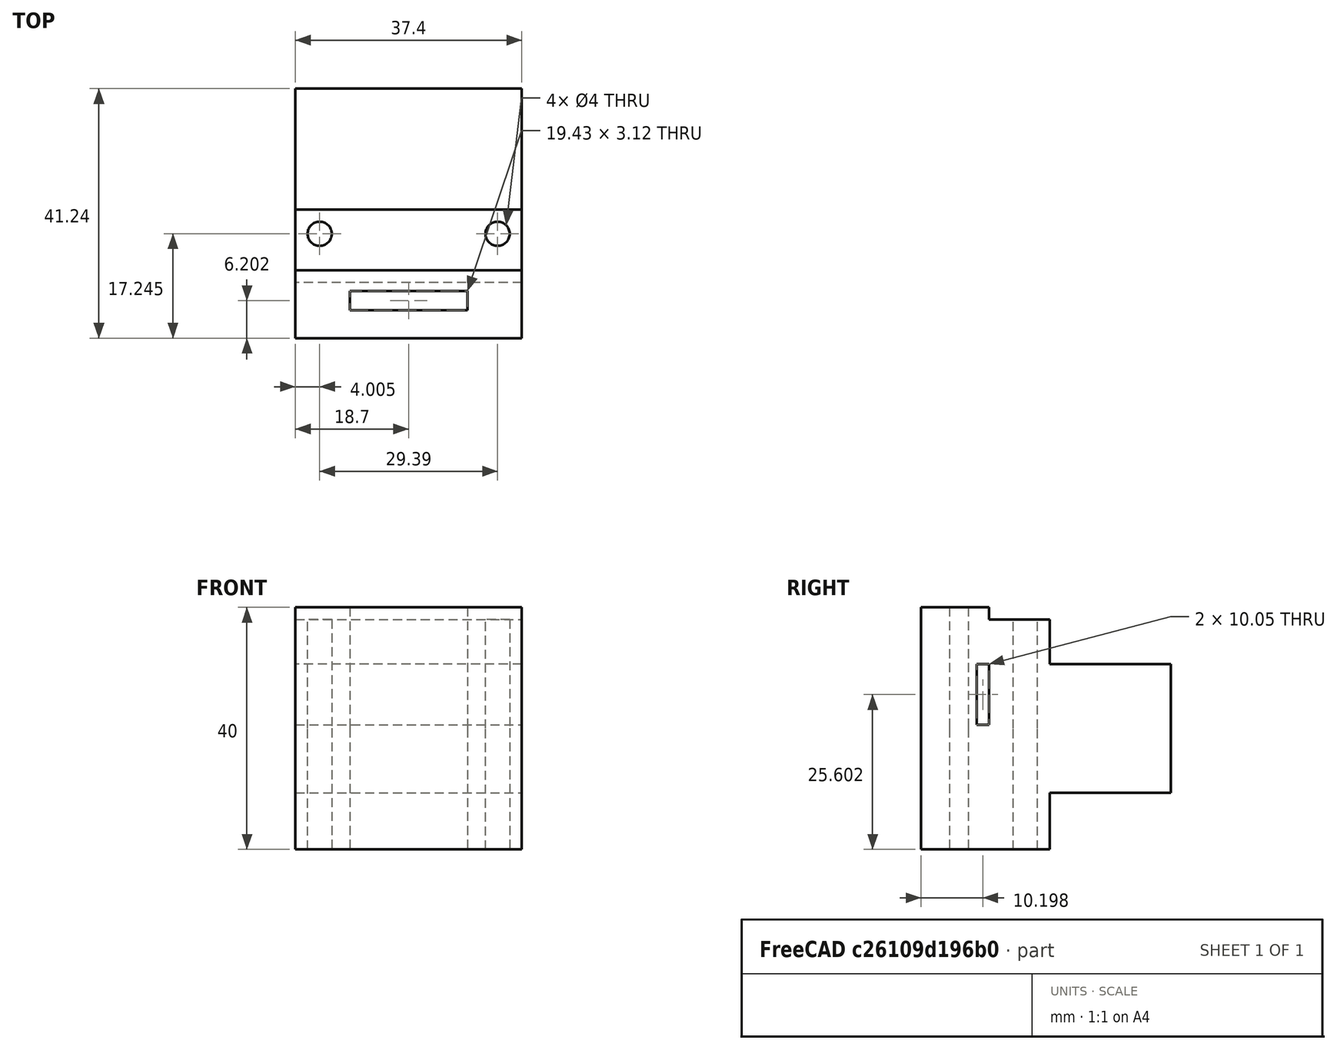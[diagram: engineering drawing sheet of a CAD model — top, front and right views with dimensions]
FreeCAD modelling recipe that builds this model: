
FCSTD DOCUMENT  (FreeCAD 0.17R13541 (Git))
Label: suporMicroSD
License: All rights reserved
LicenseURL: http://en.wikipedia.org/wiki/All_rights_reserved
objects: Sketcher::SketchObject×3, PartDesign::Body×1, PartDesign::Pad×1, PartDesign::Pocket×1
note: 8 computed .brp shape members not serialized (recipe doc carries the construction recipe); baked Part::Feature solids carry a one-line shape summary decoded from their .brp

FEATURE [PartDesign::Body] Body
  Group = -> [Sketch,Pad,Sketch001,Sketch003,Pocket001]
  Origin = -> Origin
  Tip = -> Pocket001
FEATURE [Sketcher::SketchObject] Sketch  label="base"
  MapMode = 5
  Placement = pos=(0,10.625,0) rot=(0,0.707107,0.707107;3.14159rad)
  Support = -> [Pocket001]
  sketch-geometry (4):
    g0: LineSegment StartX=-18.695 StartY=10.625 StartZ=0 EndX=18.695 EndY=10.625 EndZ=0
    g1: LineSegment StartX=18.695 StartY=10.625 StartZ=0 EndX=18.695 EndY=-10.625 EndZ=0
    g2: LineSegment StartX=18.695 StartY=-10.625 StartZ=0 EndX=-18.695 EndY=-10.625 EndZ=0
    g3: LineSegment StartX=-18.695 StartY=-10.625 StartZ=0 EndX=-18.695 EndY=10.625 EndZ=0
  constraints (12):
    c: Coincident(g0,g1)
    c: Coincident(g1,g2)
    c: Coincident(g2,g3)
    c: Coincident(g3,g0)
    c: Horizontal(g0)
    c: Horizontal(g2)
    c: Vertical(g1)
    c: Vertical(g3)
    c: Symmetric(g0,g0,g-2)
    c: Symmetric(g0,g2,g-1)
    c: DistanceX(g2,g2) = 37.39
    c: DistanceY(g1,g1) = 21.25
FEATURE [PartDesign::Pad] Pad
  Length = 20
  Length2 = 100
  Profile = -> Sketch
  Type = 0
FEATURE [Sketcher::SketchObject] Sketch001  label="trous"
  ExternalGeometry = -> [Pad]
  MapMode = 5
  Placement = pos=(0,0,20) rot=(0,0,1;0rad)
  Support = -> [Pad]
  sketch-geometry (7):
    g0: LineSegment StartX=-9.71355 StartY=-2.85593 StartZ=0 EndX=9.71355 EndY=-2.85593 EndZ=0
    g1: LineSegment StartX=9.71355 StartY=-2.85593 StartZ=0 EndX=9.71355 EndY=-5.97896 EndZ=0
    g2: LineSegment StartX=9.71355 StartY=-5.97896 StartZ=0 EndX=-9.71355 EndY=-5.97896 EndZ=0
    g3: LineSegment StartX=-9.71355 StartY=-5.97896 StartZ=0 EndX=-9.71355 EndY=-2.85593 EndZ=0
    g4: Circle CenterX=-14.695 CenterY=6.625 CenterZ=0 NormalX=0 NormalY=0 NormalZ=1 AngleXU=0 Radius=2
    g5: Circle CenterX=14.695 CenterY=6.625 CenterZ=0 NormalX=0 NormalY=0 NormalZ=1 AngleXU=0 Radius=2
    g6: LineSegment [constr] StartX=-26.587 StartY=6.625 StartZ=0 EndX=16.4781 EndY=6.625 EndZ=0
  constraints (17):
    c: Coincident(g0,g1)
    c: Coincident(g1,g2)
    c: Coincident(g2,g3)
    c: Coincident(g3,g0)
    c: Horizontal(g0)
    c: Horizontal(g2)
    c: Vertical(g1)
    c: Vertical(g3)
    c: Symmetric(g0,g0,g-2)
    c: Horizontal(g6)
    c: PointOnObject(g4,g6)
    c: PointOnObject(g5,g6)
    c: Radius(g4) = 2
    c: Radius(g5) = 2
    c: DistanceY(g6,g-3) = 4
    c: DistanceX(g-3,g4) = 4
    c: DistanceX(g5,g-3) = 4
FEATURE [Sketcher::SketchObject] Sketch003
  ExternalGeometry = -> [Sketch]
  MapMode = 5
  Placement = pos=(0,0.578362,0) rot=(0,0.707107,0.707107;3.14159rad)
  sketch-geometry (4):
    g0: LineSegment StartX=-18.695 StartY=10.625 StartZ=0 EndX=18.695 EndY=10.625 EndZ=0
    g1: LineSegment StartX=18.695 StartY=10.625 StartZ=0 EndX=18.695 EndY=0.578362 EndZ=0
    g2: LineSegment StartX=18.695 StartY=0.578362 StartZ=0 EndX=-18.695 EndY=0.578362 EndZ=0
    g3: LineSegment StartX=-18.695 StartY=0.578362 StartZ=0 EndX=-18.695 EndY=10.625 EndZ=0
  constraints (10):
    c: Coincident(g0,g1)
    c: Coincident(g1,g2)
    c: Coincident(g2,g3)
    c: Coincident(g3,g0)
    c: Horizontal(g0)
    c: Horizontal(g2)
    c: Vertical(g1)
    c: Vertical(g3)
    c: Coincident(g0,g-3)
    c: Coincident(g-4,g0)
FEATURE [PartDesign::Pocket] Pocket001
  BaseFeature = -> Pad
  Length = 2
  Length2 = 100
  Profile = -> Sketch003
  Type = 0
